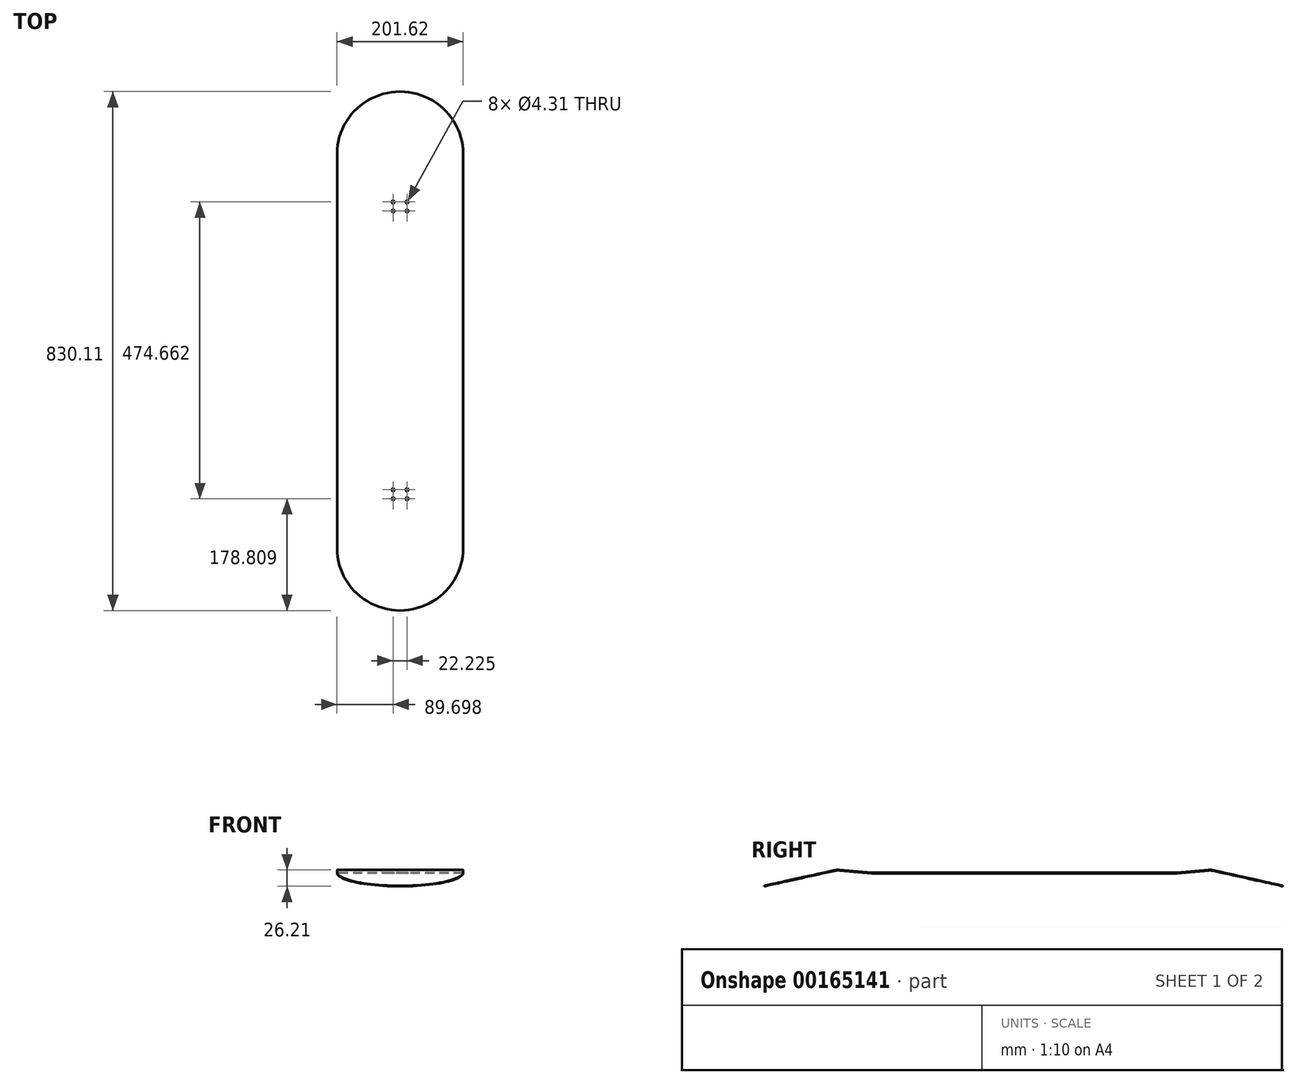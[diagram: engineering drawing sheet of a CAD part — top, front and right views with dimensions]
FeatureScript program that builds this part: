
annotation { "Feature Type Name" : "Feature", "Feature Type Description" : "" }
export const myFeature = defineFeature(function(context is Context, id is Id, definition is map)
    precondition{}
    {
        {
            var Q0;
            Q0=qCreatedBy(makeId("Top.planeOp"),FACE);
            var sketch = newSketch(context, id + "F0", { "sketchPlane" : qUnion([Q0])});
            skLineSegment(sketch, "E0.bottom", {"start": v(100.8, 241.3) * mm, "end": v(-100.8, 241.3) * mm});
            skLineSegment(sketch, "E0.top", {"start": v(100.8, -241.3) * mm, "end": v(-100.8, -241.3) * mm});
            skLineSegment(sketch, "E0.left", {"start": v(100.8, 241.3) * mm, "end": v(100.8, -241.3) * mm});
            skLineSegment(sketch, "E0.right", {"start": v(-100.8, 241.3) * mm, "end": v(-100.8, -241.3) * mm});
            skPoint(sketch, "E0.middle", {"position": v(0, 0) * mm});
            skSolve(sketch);
        }
        {
            var Q0;
            Q0=makeQuery(id+"F0.imprint","IMPRINT",FACE,{"disambiguationData":[TD([[makeQuery(id+"F0.imprint","IMPRINT",EDGE,{"derivedFrom":sQuery(id+"F0.wireOp",EDGE,"E0.bottom")}),1.0]])]});
            extrude(context, id + "F1", {"entities" : qUnion([Q0]), "depth" : 0.8 * mm});
        }
        {
            var Q0;
            Q0=makeQuery(id+"F1.opExtrude","SWEPT_FACE",FACE,{"disambiguationData":[OSD([sQuery(id+"F0.wireOp",EDGE,"E0.left")])]});
            var sketch = newSketch(context, id + "F2", { "sketchPlane" : qUnion([Q0])});
            skLineSegment(sketch, "E1", {"start": v(241.3, 0.8) * mm, "end": v(241.3, 0) * mm});
            skArc(sketch, "E2", {"start": v(241.3, 0) * mm, "mid": v(242.72, 0.03) * mm, "end": v(244.14, 0.12) * mm});
            skArc(sketch, "E3", {"start": v(241.3, 0.8) * mm, "mid": v(242.68, 0.82) * mm, "end": v(244.07, 0.91) * mm});
            skLineSegment(sketch, "E4", {"start": v(241.3, 0) * mm, "end": v(296.89, 0) * mm, "construction": true});
            skLineSegment(sketch, "E5.bottom", {"start": v(244.07, 0.91) * mm, "end": v(294.67, 5.34) * mm});
            skLineSegment(sketch, "E5.top", {"start": v(244.14, 0.12) * mm, "end": v(294.74, 4.55) * mm});
            skLineSegment(sketch, "E5.left", {"start": v(244.07, 0.91) * mm, "end": v(244.14, 0.12) * mm, "construction": true});
            skLineSegment(sketch, "E5.right", {"start": v(294.67, 5.34) * mm, "end": v(294.74, 4.55) * mm, "construction": true});
            skLineSegment(sketch, "E6", {"start": v(241.3, 32.54) * mm, "end": v(244.07, 0.91) * mm, "construction": true});
            skArc(sketch, "E7", {"start": v(302.23, 4.06) * mm, "mid": v(298.5, 4.6) * mm, "end": v(294.74, 4.55) * mm});
            skArc(sketch, "E8", {"start": v(302.4, 4.83) * mm, "mid": v(298.56, 5.38) * mm, "end": v(294.67, 5.34) * mm});
            skLineSegment(sketch, "E9.bottom", {"start": v(302.23, 4.06) * mm, "end": v(413.8, -20.74) * mm});
            skLineSegment(sketch, "E9.top", {"start": v(302.4, 4.83) * mm, "end": v(413.98, -19.96) * mm});
            skLineSegment(sketch, "E9.left", {"start": v(302.23, 4.06) * mm, "end": v(302.4, 4.83) * mm, "construction": true});
            skLineSegment(sketch, "E9.right", {"start": v(413.8, -20.74) * mm, "end": v(413.98, -19.96) * mm});
            skLineSegment(sketch, "E10", {"start": v(296.89, 5.44) * mm, "end": v(413.98, 5.44) * mm, "construction": true});
            skLineSegment(sketch, "E11", {"start": v(413.98, 5.44) * mm, "end": v(413.98, -19.96) * mm, "construction": true});
            skLineSegment(sketch, "E12", {"start": v(296.89, 0) * mm, "end": v(296.89, 5.44) * mm, "construction": true});
            skArc(sketch, "E13", {"start": v(-244.14, 0.12) * mm, "mid": v(-242.72, 0.03) * mm, "end": v(-241.3, 0) * mm});
            skArc(sketch, "E14", {"start": v(-244.07, 0.91) * mm, "mid": v(-242.68, 0.82) * mm, "end": v(-241.3, 0.8) * mm});
            skLineSegment(sketch, "E15", {"start": v(-241.3, 0) * mm, "end": v(-241.3, 0.8) * mm});
            skLineSegment(sketch, "E16.bottom", {"start": v(-244.14, 0.12) * mm, "end": v(-294.74, 4.55) * mm});
            skLineSegment(sketch, "E16.top", {"start": v(-244.07, 0.91) * mm, "end": v(-294.67, 5.34) * mm});
            skLineSegment(sketch, "E16.left", {"start": v(-244.14, 0.12) * mm, "end": v(-244.07, 0.91) * mm, "construction": true});
            skLineSegment(sketch, "E16.right", {"start": v(-294.74, 4.55) * mm, "end": v(-294.67, 5.34) * mm, "construction": true});
            skArc(sketch, "E17", {"start": v(-294.74, 4.55) * mm, "mid": v(-299.58, 4.6) * mm, "end": v(-304.36, 3.92) * mm});
            skArc(sketch, "E18", {"start": v(-294.67, 5.34) * mm, "mid": v(-299.63, 5.4) * mm, "end": v(-304.53, 4.7) * mm});
            skLineSegment(sketch, "E19.bottom", {"start": v(-304.36, 3.92) * mm, "end": v(-415.97, -20.74) * mm});
            skLineSegment(sketch, "E19.top", {"start": v(-304.53, 4.7) * mm, "end": v(-416.14, -19.96) * mm});
            skLineSegment(sketch, "E19.left", {"start": v(-304.36, 3.92) * mm, "end": v(-304.53, 4.7) * mm, "construction": true});
            skLineSegment(sketch, "E19.right", {"start": v(-415.97, -20.74) * mm, "end": v(-416.14, -19.96) * mm});
            skLineSegment(sketch, "E20", {"start": v(294.74, 4.55) * mm, "end": v(-294.74, 4.55) * mm, "construction": true});
            skLineSegment(sketch, "E21", {"start": v(0, 4.55) * mm, "end": v(0, 0.8) * mm, "construction": true});
            skLineSegment(sketch, "E22", {"start": v(413.8, -20.74) * mm, "end": v(-415.97, -20.74) * mm, "construction": true});
            skSolve(sketch);
        }
        {
            var Q0;
            Q0=makeQuery(id+"F2.imprint","IMPRINT",FACE,{"disambiguationData":[TD([[makeQuery(id+"F2.imprint","IMPRINT",EDGE,{"derivedFrom":sQuery(id+"F2.wireOp",EDGE,"E1")}),1.0]])]});
            var Q1;
            Q1=makeQuery(id+"F2.imprint","IMPRINT",FACE,{"disambiguationData":[TD([[makeQuery(id+"F2.imprint","IMPRINT",EDGE,{"derivedFrom":sQuery(id+"F2.wireOp",EDGE,"E13")}),1.0]])]});
            var Q2;
            Q2=makeQuery(id+"F1.opExtrude","SWEPT_FACE",FACE,{"disambiguationData":[OSD([sQuery(id+"F0.wireOp",EDGE,"E0.right")])]});
            extrude(context, id + "F3", {"entities" : qUnion([Q0, Q1]), "operationType" : NewBodyOperationType.ADD, "endBound" : BoundingType.UP_TO_SURFACE, "oppositeDirection" : true, "endBoundEntityFace" : qUnion([Q2]), "depth" : 25.4 * mm});
        }
        {
            var Q0;
            Q0=makeQuery(id+"F3.opExtrude","CAP_EDGE",EDGE,{"disambiguationData":[OSD([sQuery(id+"F2.wireOp",EDGE,"E9.right")])],"isStart":true});
            var Q1;
            Q1=makeQuery(id+"F3.opExtrude","CAP_EDGE",EDGE,{"disambiguationData":[OSD([sQuery(id+"F2.wireOp",EDGE,"E9.right")])],"isStart":false});
            var Q2;
            Q2=makeQuery(id+"F3.opExtrude","CAP_EDGE",EDGE,{"disambiguationData":[OSD([sQuery(id+"F2.wireOp",EDGE,"E19.right")])],"isStart":true});
            var Q3;
            Q3=makeQuery(id+"F3.opExtrude","CAP_EDGE",EDGE,{"disambiguationData":[OSD([sQuery(id+"F2.wireOp",EDGE,"E19.right")])],"isStart":false});
            fillet(context, id + "F4", {"entities" : qUnion([Q0, Q1, Q2, Q3]), "radius" : 101.6 * mm, "tangentPropagation" : true, "allowEdgeOverflow" : false});
        }
        {
            var Q0;
            Q0=makeQuery(id+"F1.opExtrude","CAP_FACE",FACE,{"disambiguationData":[OSD([sQuery(id+"F0.wireOp",EDGE,"E0.bottom"),sQuery(id+"F0.wireOp",EDGE,"E0.top"),sQuery(id+"F0.wireOp",EDGE,"E0.left"),sQuery(id+"F0.wireOp",EDGE,"E0.right")])],"isStart":false});
            var sketch = newSketch(context, id + "F5", { "sketchPlane" : qUnion([Q0])});
            skLineSegment(sketch, "E23", {"start": v(0, 241.3) * mm, "end": v(0, 237.33) * mm, "construction": true});
            skLineSegment(sketch, "E24", {"start": v(0, -241.3) * mm, "end": v(0, -237.33) * mm, "construction": true});
            skLineSegment(sketch, "E25.bottom", {"start": v(-11.11, 237.33) * mm, "end": v(11.11, 237.33) * mm, "construction": true});
            skLineSegment(sketch, "E25.top", {"start": v(-11.11, 223.04) * mm, "end": v(11.11, 223.04) * mm, "construction": true});
            skLineSegment(sketch, "E25.left", {"start": v(-11.11, 237.33) * mm, "end": v(-11.11, 223.04) * mm, "construction": true});
            skLineSegment(sketch, "E25.right", {"start": v(11.11, 237.33) * mm, "end": v(11.11, 223.04) * mm, "construction": true});
            skLineSegment(sketch, "E26.bottom", {"start": v(-11.11, -237.33) * mm, "end": v(11.11, -237.33) * mm, "construction": true});
            skLineSegment(sketch, "E26.top", {"start": v(-11.11, -223.04) * mm, "end": v(11.11, -223.04) * mm, "construction": true});
            skLineSegment(sketch, "E26.left", {"start": v(-11.11, -237.33) * mm, "end": v(-11.11, -223.04) * mm, "construction": true});
            skLineSegment(sketch, "E26.right", {"start": v(11.11, -237.33) * mm, "end": v(11.11, -223.04) * mm, "construction": true});
            skCircle(sketch, "E27", {"center": v(-11.11, 237.33) * mm, "radius": 2.15 * mm});
            skCircle(sketch, "E28", {"center": v(11.11, 237.33) * mm, "radius": 2.15 * mm});
            skCircle(sketch, "E29", {"center": v(11.11, 223.04) * mm, "radius": 2.15 * mm});
            skCircle(sketch, "E30", {"center": v(-11.11, 223.04) * mm, "radius": 2.15 * mm});
            skCircle(sketch, "E31", {"center": v(11.11, -223.04) * mm, "radius": 2.15 * mm});
            skCircle(sketch, "E32", {"center": v(-11.11, -223.04) * mm, "radius": 2.15 * mm});
            skCircle(sketch, "E33", {"center": v(-11.11, -237.33) * mm, "radius": 2.15 * mm});
            skCircle(sketch, "E34", {"center": v(11.11, -237.33) * mm, "radius": 2.15 * mm});
            skPoint(sketch, "E35", {"position": v(-11.11, -230.19) * mm});
            skPoint(sketch, "E36", {"position": v(-11.11, 230.19) * mm});
            skSolve(sketch);
        }
        {
            var Q0;
            Q0=qSketchRegion(id+"F5",true);
            var Q1;
            Q1=makeQuery(id+"F1.opExtrude","CAP_FACE",FACE,{"disambiguationData":[OSD([sQuery(id+"F0.wireOp",EDGE,"E0.bottom"),sQuery(id+"F0.wireOp",EDGE,"E0.top"),sQuery(id+"F0.wireOp",EDGE,"E0.left"),sQuery(id+"F0.wireOp",EDGE,"E0.right")])],"isStart":true});
            extrude(context, id + "F6", {"entities" : qUnion([Q0]), "operationType" : NewBodyOperationType.REMOVE, "endBound" : BoundingType.UP_TO_SURFACE, "oppositeDirection" : true, "endBoundEntityFace" : qUnion([Q1]), "depth" : 25.4 * mm});
        }
    });
